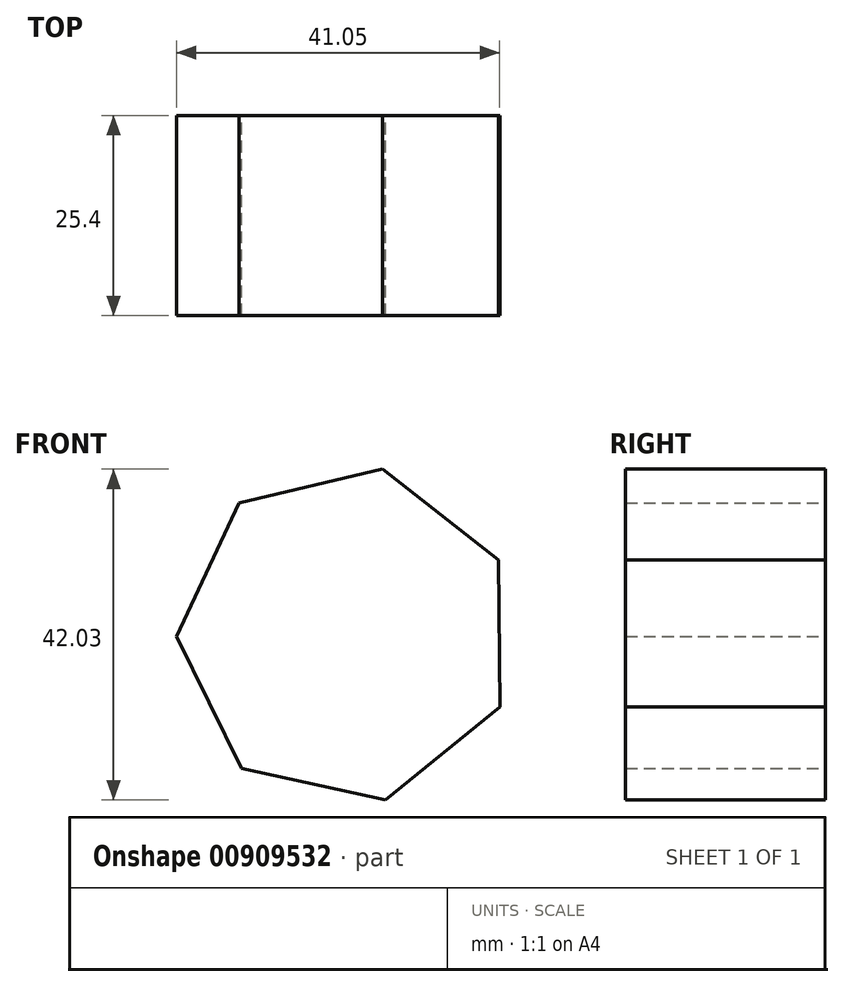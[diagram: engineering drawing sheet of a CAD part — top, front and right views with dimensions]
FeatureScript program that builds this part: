
annotation { "Feature Type Name" : "Feature", "Feature Type Description" : "" }
export const myFeature = defineFeature(function(context is Context, id is Id, definition is map)
    precondition{}
    {
        {
            var Q0;
            Q0=qCreatedBy(makeId("Front.planeOp"),FACE);
            var sketch = newSketch(context, id + "F0", { "sketchPlane" : qUnion([Q0])});
            skCircle(sketch, "E0.cCircle", {"center": v(-69.64, 46.08) * mm, "radius": 19.42 * mm, "construction": true});
            skLineSegment(sketch, "E0.0", {"start": v(-50.14, 36.9) * mm, "end": v(-64.66, 25.11) * mm});
            skLineSegment(sketch, "E0.1", {"start": v(-64.66, 25.11) * mm, "end": v(-82.93, 29.11) * mm});
            skLineSegment(sketch, "E0.2", {"start": v(-82.93, 29.11) * mm, "end": v(-91.2, 45.9) * mm});
            skLineSegment(sketch, "E0.3", {"start": v(-91.2, 45.9) * mm, "end": v(-83.23, 62.82) * mm});
            skLineSegment(sketch, "E0.4", {"start": v(-83.23, 62.82) * mm, "end": v(-65.03, 67.14) * mm});
            skLineSegment(sketch, "E0.5", {"start": v(-65.03, 67.14) * mm, "end": v(-50.3, 55.6) * mm});
            skLineSegment(sketch, "E0.6", {"start": v(-50.3, 55.6) * mm, "end": v(-50.14, 36.9) * mm});
            skPoint(sketch, "E0.0.midPoint", {"position": v(-57.4, 31.01) * mm});
            skSolve(sketch);
        }
        {
            var Q0;
            Q0=makeQuery(id+"F0.imprint","IMPRINT",FACE,{"disambiguationData":[TD([[makeQuery(id+"F0.imprint","IMPRINT",EDGE,{"derivedFrom":sQuery(id+"F0.wireOp",EDGE,"E0.0")}),-1.0]])]});
            extrude(context, id + "F1", {"entities" : qUnion([Q0]), "depth" : 25.4 * mm, "offsetDistance" : 25.4 * mm});
        }
    });
